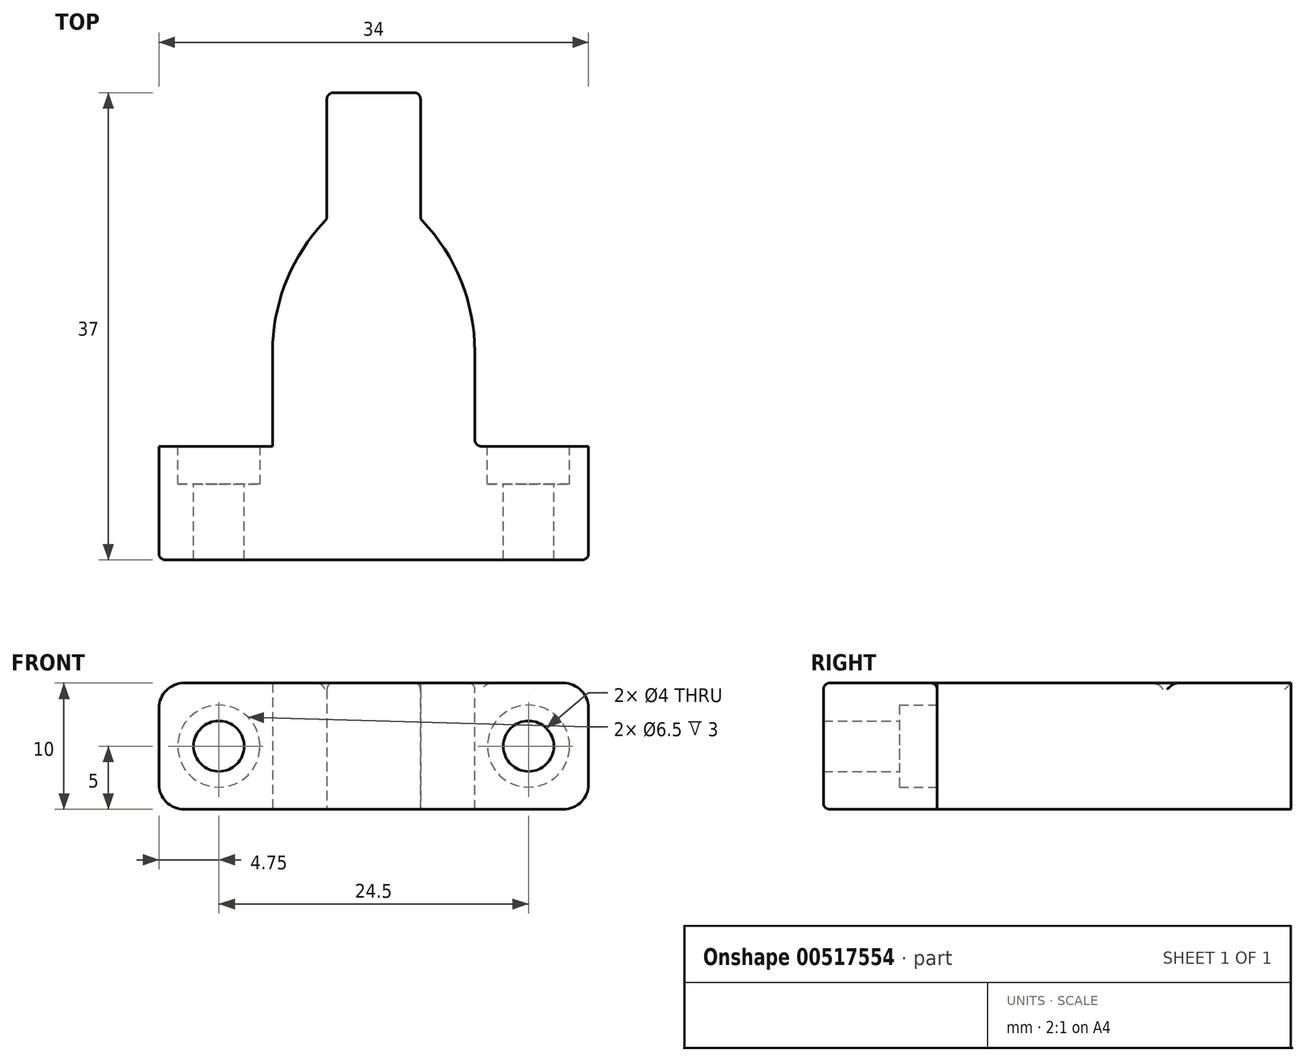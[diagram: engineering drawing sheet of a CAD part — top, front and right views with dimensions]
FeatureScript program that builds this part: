
annotation { "Feature Type Name" : "Feature", "Feature Type Description" : "" }
export const myFeature = defineFeature(function(context is Context, id is Id, definition is map)
    precondition{}
    {
        {
            var Q0;
            Q0=qCreatedBy(makeId("Front.planeOp"),FACE);
            var sketch = newSketch(context, id + "F0", { "sketchPlane" : qUnion([Q0])});
            skLineSegment(sketch, "E0.bottom", {"start": v(0, 0) * mm, "end": v(-34, 0) * mm});
            skLineSegment(sketch, "E0.top", {"start": v(0, 10) * mm, "end": v(-34, 10) * mm});
            skLineSegment(sketch, "E0.left", {"start": v(0, 0) * mm, "end": v(0, 10) * mm});
            skLineSegment(sketch, "E0.right", {"start": v(-34, 0) * mm, "end": v(-34, 10) * mm});
            skLineSegment(sketch, "E1", {"start": v(-34, 5) * mm, "end": v(0, 5) * mm, "construction": true});
            skPoint(sketch, "E2", {"position": v(-29.25, 5) * mm});
            skPoint(sketch, "E3", {"position": v(-4.75, 5) * mm});
            skLineSegment(sketch, "E4", {"start": v(-25, 10) * mm, "end": v(-25, 0) * mm});
            skLineSegment(sketch, "E5", {"start": v(-13.3, 0) * mm, "end": v(-13.3, 10) * mm});
            skLineSegment(sketch, "E6", {"start": v(-13.3, 10) * mm, "end": v(-20.7, 10) * mm});
            skLineSegment(sketch, "E7", {"start": v(-20.7, 10) * mm, "end": v(-20.7, 0) * mm});
            skLineSegment(sketch, "E8", {"start": v(-17, 5) * mm, "end": v(-17, 10) * mm, "construction": true});
            skLineSegment(sketch, "E9.MirrorCS", {"start": v(-9, 10) * mm, "end": v(-9, 0) * mm});
            skSolve(sketch);
        }
        {
            var Q0;
            Q0 = qSketchRegion(id + "F0", true);
            extrude(context, id + "F1", {"entities" : qUnion([Q0]), "depth" : 9 * mm, "offsetDistance" : 25 * mm});
        }
        {
            var Q0;
            Q0=sQuery(id+"F0.wireOp",VERTEX,"E2");
            var Q1;
            Q1=sQuery(id+"F0.wireOp",VERTEX,"E3");
            var Q2;
            Q2=makeQuery(id+"F1.opExtrude","SWEPT_BODY",BODY,{"disambiguationData":[OSD([sQuery(id+"F0.wireOp",EDGE,"E0.bottom"),sQuery(id+"F0.wireOp",EDGE,"E0.top"),sQuery(id+"F0.wireOp",EDGE,"E0.left"),sQuery(id+"F0.wireOp",EDGE,"E0.right")])]});
            hole(context, id + "F2", {"style" : HoleStyle.C_BORE, "endStyle" : HoleEndStyle.BLIND, "oppositeDirection" : true, "holeDiameter" : 4 * mm, "cBoreDiameter" : 6.5 * mm, "cBoreDepth" : 3 * mm, "majorDiameter" : 5 * mm, "holeDepth" : 12 * mm, "isTappedThrough" : true, "tappedDepth" : 12 * mm, "tapClearance" : 3, "locations" : qUnion([Q0, Q1]), "scope" : qUnion([Q2])});
        }
        {
            var Q0;
            {var subQ0=sQuery(id+"F0.wireOp",EDGE,"E4");Q0=makeQuery(id+"F0.imprint","IMPRINT",FACE,{"disambiguationData":[TD([[makeQuery(id+"F0.imprint","IMPRINT",EDGE,{"derivedFrom":subQ0}),1.0]])]});}
            var Q1;
            {var subQ0=sQuery(id+"F0.wireOp",EDGE,"E5");Q1=makeQuery(id+"F0.imprint","IMPRINT",FACE,{"disambiguationData":[TD([[makeQuery(id+"F0.imprint","IMPRINT",EDGE,{"derivedFrom":subQ0}),1.0]])]});}
            var Q2;
            {var subQ0=sQuery(id+"F0.wireOp",EDGE,"E5");Q2=makeQuery(id+"F0.imprint","IMPRINT",FACE,{"disambiguationData":[TD([[makeQuery(id+"F0.imprint","IMPRINT",EDGE,{"derivedFrom":subQ0}),-1.0]])]});}
            extrude(context, id + "F3", {"entities" : qUnion([Q0, Q1, Q2]), "operationType" : NewBodyOperationType.ADD, "oppositeDirection" : true, "depth" : (28 - 10) * mm, "offsetDistance" : 25 * mm});
        }
        {
            var Q0;
            {var subQ0=sQuery(id+"F0.wireOp",EDGE,"E5");Q0=makeQuery(id+"F0.imprint","IMPRINT",FACE,{"disambiguationData":[TD([[makeQuery(id+"F0.imprint","IMPRINT",EDGE,{"derivedFrom":subQ0}),1.0]])]});}
            extrude(context, id + "F4", {"entities" : qUnion([Q0]), "operationType" : NewBodyOperationType.ADD, "oppositeDirection" : true, "depth" : 28 * mm, "offsetDistance" : 25 * mm});
        }
        {
            var Q0;
            Q0=makeQuery(id+"F3.opExtrude","CAP_EDGE",EDGE,{"disambiguationData":[OSD([sQuery(id+"F0.wireOp",EDGE,"E9.MirrorCS")])],"isStart":false});
            var Q1;
            Q1=makeQuery(id+"F3.opExtrude","CAP_EDGE",EDGE,{"disambiguationData":[OSD([sQuery(id+"F0.wireOp",EDGE,"E4")])],"isStart":false});
            fillet(context, id + "F5", {"entities" : qUnion([Q0, Q1]), "radius" : 15 * mm, "tangentPropagation" : true, "allowEdgeOverflow" : false});
        }
        {
            var Q0;
            Q0=makeQuery(id+"F1.opExtrude","SWEPT_EDGE",EDGE,{"disambiguationData":[OSD([sQuery(id+"F0.wireOp",EDGE,"E0.top"),sQuery(id+"F0.wireOp",EDGE,"E0.left")])]});
            var Q1;
            Q1=makeQuery(id+"F1.opExtrude","SWEPT_EDGE",EDGE,{"disambiguationData":[OSD([sQuery(id+"F0.wireOp",EDGE,"E0.bottom"),sQuery(id+"F0.wireOp",EDGE,"E0.left")])]});
            var Q2;
            Q2=makeQuery(id+"F1.opExtrude","SWEPT_EDGE",EDGE,{"disambiguationData":[OSD([sQuery(id+"F0.wireOp",EDGE,"E0.bottom"),sQuery(id+"F0.wireOp",EDGE,"E0.right")])]});
            var Q3;
            Q3=makeQuery(id+"F1.opExtrude","SWEPT_EDGE",EDGE,{"disambiguationData":[OSD([sQuery(id+"F0.wireOp",EDGE,"E0.top"),sQuery(id+"F0.wireOp",EDGE,"E0.right")])]});
            fillet(context, id + "F6", {"entities" : qUnion([Q0, Q1, Q2, Q3]), "radius" : 2 * mm, "tangentPropagation" : true, "allowEdgeOverflow" : false});
        }
        {
            var Q0;
            Q0=makeQuery(id+"F3.opExtrude","CAP_EDGE",EDGE,{"disambiguationData":[OSD([sQuery(id+"F0.wireOp",EDGE,"E9.MirrorCS")])],"isStart":true});
            var Q1;
            Q1=makeQuery(id+"F3.opExtrude","CAP_EDGE",EDGE,{"disambiguationData":[OSD([sQuery(id+"F0.wireOp",EDGE,"E4")])],"isStart":true});
            var Q2;
            {var subQ0=sQuery(id+"F0.wireOp",EDGE,"E4");Q2=makeQuery(id+"F5.opFillet","BLEND_EDGE",EDGE,{"blendedFrom":[makeQuery(id+"F3.opExtrude","CAP_EDGE",EDGE,{"disambiguationData":[OSD([subQ0])],"isStart":false}),makeQuery(id+"F3.opExtrude","SWEPT_FACE",FACE,{"disambiguationData":[OSD([subQ0])]})],"blendedInto":[makeQuery(id+"F3.opExtrude","SWEPT_FACE",FACE,{"disambiguationData":[OSD([subQ0])]})]});}
            var Q3;
            Q3=makeQuery(id+"F5.opFillet","BLEND_EDGE",EDGE,{"blendedFrom":[makeQuery(id+"F3.opExtrude","CAP_EDGE",EDGE,{"disambiguationData":[OSD([sQuery(id+"F0.wireOp",EDGE,"E4")])],"isStart":false}),makeQuery(id+"F4.opExtrude","SWEPT_FACE",FACE,{"disambiguationData":[OSD([sQuery(id+"F0.wireOp",EDGE,"E7")])]})],"blendedInto":[makeQuery(id+"F4.opExtrude","SWEPT_FACE",FACE,{"disambiguationData":[OSD([sQuery(id+"F0.wireOp",EDGE,"E7")])]})]});
            var Q4;
            Q4=makeQuery(id+"F5.opFillet","BLEND_EDGE",EDGE,{"blendedFrom":[makeQuery(id+"F3.opExtrude","CAP_EDGE",EDGE,{"disambiguationData":[OSD([sQuery(id+"F0.wireOp",EDGE,"E9.MirrorCS")])],"isStart":false}),makeQuery(id+"F4.opExtrude","SWEPT_FACE",FACE,{"disambiguationData":[OSD([sQuery(id+"F0.wireOp",EDGE,"E5")])]})],"blendedInto":[makeQuery(id+"F4.opExtrude","SWEPT_FACE",FACE,{"disambiguationData":[OSD([sQuery(id+"F0.wireOp",EDGE,"E5")])]})]});
            var Q5;
            Q5=makeQuery(id+"F4.opExtrude","CAP_EDGE",EDGE,{"disambiguationData":[OSD([sQuery(id+"F0.wireOp",EDGE,"E5")])],"isStart":false});
            var Q6;
            Q6=makeQuery(id+"F4.opExtrude","CAP_EDGE",EDGE,{"disambiguationData":[OSD([sQuery(id+"F0.wireOp",EDGE,"E7")])],"isStart":false});
            var Q7;
            Q7=makeQuery(id+"F4.opExtrude","CAP_EDGE",EDGE,{"disambiguationData":[OSD([sQuery(id+"F0.wireOp",EDGE,"E6")])],"isStart":false});
            var Q8;
            Q8=makeQuery(id+"F4.opExtrude","SWEPT_EDGE",EDGE,{"disambiguationData":[OSD([sQuery(id+"F0.wireOp",EDGE,"E0.top"),sQuery(id+"F0.wireOp",EDGE,"E6"),sQuery(id+"F0.wireOp",EDGE,"E7")])]});
            var Q9;
            {var subQ0=sQuery(id+"F0.wireOp",EDGE,"E6");var subQ1=sQuery(id+"F0.wireOp",EDGE,"E0.top");Q9=makeQuery(id+"F5.opFillet","BLEND_EDGE",EDGE,{"blendedFrom":[makeQuery(id+"F3.opExtrude","CAP_EDGE",EDGE,{"disambiguationData":[OSD([sQuery(id+"F0.wireOp",EDGE,"E9.MirrorCS")])],"isStart":false}),makeQuery(id+"F4.boolean.opBoolean","MERGE",FACE,{"derivedFrom":[makeQuery(id+"F3.boolean.opBoolean","MERGE",FACE,{"derivedFrom":[makeQuery(id+"F1.opExtrude","SWEPT_FACE",FACE,{"disambiguationData":[OSD([subQ1,subQ0])]}),makeQuery(id+"F3.opExtrude","SWEPT_FACE",FACE,{"disambiguationData":[OSD([subQ1,subQ0])]})]}),makeQuery(id+"F4.opExtrude","SWEPT_FACE",FACE,{"disambiguationData":[OSD([subQ0])]})]})],"blendedInto":[makeQuery(id+"F4.boolean.opBoolean","MERGE",FACE,{"derivedFrom":[makeQuery(id+"F3.boolean.opBoolean","MERGE",FACE,{"derivedFrom":[makeQuery(id+"F1.opExtrude","SWEPT_FACE",FACE,{"disambiguationData":[OSD([subQ1,subQ0])]}),makeQuery(id+"F3.opExtrude","SWEPT_FACE",FACE,{"disambiguationData":[OSD([subQ1,subQ0])]})]}),makeQuery(id+"F4.opExtrude","SWEPT_FACE",FACE,{"disambiguationData":[OSD([subQ0])]})]})]});}
            var Q10;
            Q10=makeQuery(id+"F1.opExtrude","CAP_EDGE",EDGE,{"disambiguationData":[OSD([sQuery(id+"F0.wireOp",EDGE,"E0.top"),sQuery(id+"F0.wireOp",EDGE,"E6")])],"isStart":false});
            fillet(context, id + "F7", {"entities" : qUnion([Q0, Q1, Q2, Q3, Q4, Q5, Q6, Q7, Q8, Q9, Q10]), "radius" : 0.5 * mm, "tangentPropagation" : true, "allowEdgeOverflow" : false});
        }
    });
